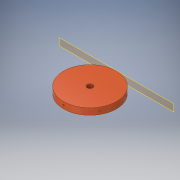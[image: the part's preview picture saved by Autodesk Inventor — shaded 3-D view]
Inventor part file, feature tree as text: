
AUTODESK INVENTOR PART (.ipt)
format: ipt  version: 2017 (Build 210142000, 142)  size: 130,560 bytes
history: native  units: in
note: dims shown in document units (in); Inventor stores cm internally (conversion verified against a paired STEP export)
features: sketch x3, revolve x1, plane x1, hole x1, pattern_circular x1, extrude x1
ambient origin geometry x8: Origin, YZ Plane, XZ Plane, XY Plane, X Axis, Y Axis, Z Axis, Center Point
bodies: Solid1 (feature_tree)
feature tree (8):
  revolve  "Revolution1"  [1 undecoded]
  plane  "Work Plane1"
  hole  "Hole1"  [1 undecoded]
  pattern_circular  "Circular Pattern1"  Count=6 Angle=360.0deg
  extrude  "Extrusion1"  Depth=0.375in
  sketch  "Sketch1"  dims[d0=3.5in d1=0.862in]
  sketch  "Sketch2"  dims[d2=90.0deg d3=0.431in]
  sketch  "Sketch3"  dims[d4=0.196in d5=0.5in d6=0.375in d7=0.25in d8=0.5635in d9=0.5in d10=0.8108in d11=2.3622in d12=360.0deg d14=0.75in d15=2.9375in d16=0.0in]
note: 2 required parameter values undecoded (feature->parameter linkage not recoverable at this tier; creation-order binding heuristic only, values carry confidence <= 0.55)